# Revit family: Gira_018200
name_source: partatom
category: Electrical Fixtures
revit_build: Autodesk Revit 2017 (Build: 20160225_1515(x64)
units: mm (PartAtom-declared; Revit-internal decimal feet)

## family parameters
Cut with Voids When Loaded = No
Host = Face
Maintain Annotation Orientation = Yes
Part Type = Normal
Room Calculation Point = No
Round Connector Dimension = Use Diameter
Shared = No

## types (1)
- Gira_018200
    Andere Bussysteme = ohne
    Available = Yes
    Befestigungsart = Krallen-/Schraubbefestigung
    Bussystem Funkbus = No
    Bussystem KNX = Yes
    Bussystem KNX-Funk = No
    Bussystem LON = No
    Bussystem Powernet = No
    Category = Bussystem-Ankoppler
    Data sheet (1) = https://katalog.gira.de
    Default Elevation = 1219 mm
    GTIN = 4010337182009
    HAN = 018200
    HeinzeBIM = https://bimportal.heinze.de
    Keynote = Einsatz_1fach
    Manufacturer URL = https://www.gira.de
    Montageart = unter Putz
    Name = Taster-BA 2f 1-Punkt KNX Einsatz
    Region = DE
    URL = http://katalog.gira.de

## geometry (parser evidence)
native form markers: Sweep x3
no freeform markers — native parametric forms only
